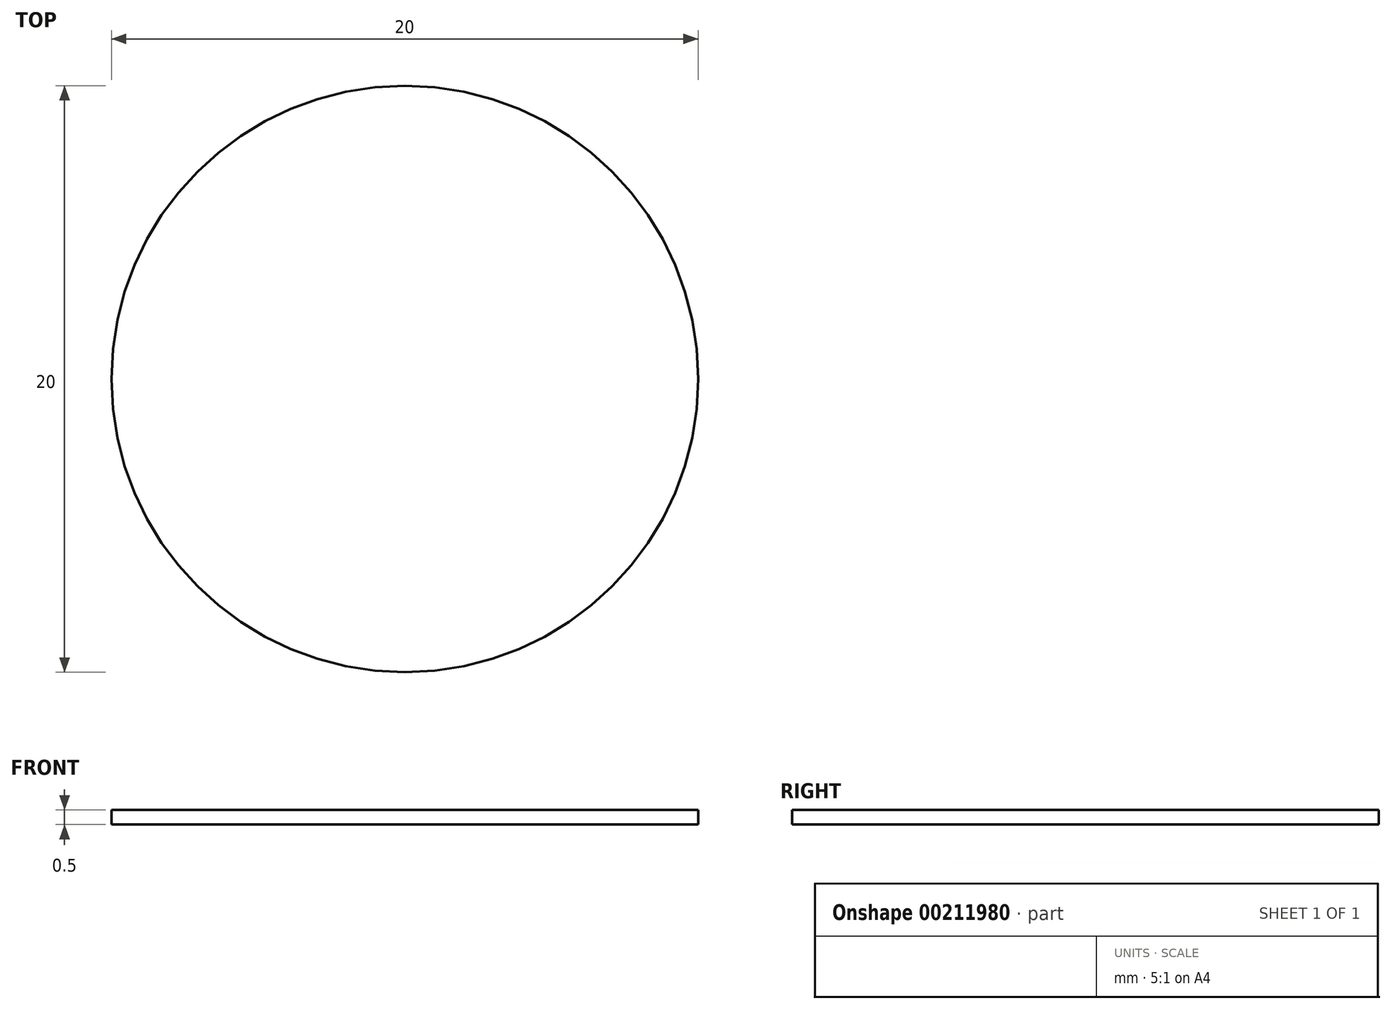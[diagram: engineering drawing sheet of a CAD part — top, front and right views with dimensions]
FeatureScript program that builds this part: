
annotation { "Feature Type Name" : "Feature", "Feature Type Description" : "" }
export const myFeature = defineFeature(function(context is Context, id is Id, definition is map)
    precondition{}
    {
        {
            var Q0;
            Q0=qCreatedBy(makeId("Top.planeOp"),FACE);
            var sketch = newSketch(context, id + "F0", { "sketchPlane" : qUnion([Q0])});
            skCircle(sketch, "E0", {"center": v(0, 0) * mm, "radius": 10 * mm});
            skSolve(sketch);
        }
        {
            var Q0;
            Q0 = qSketchRegion(id + "F0", true);
            extrude(context, id + "F1", {"entities" : qUnion([Q0]), "depth" : 0.5 * mm});
        }
    });
